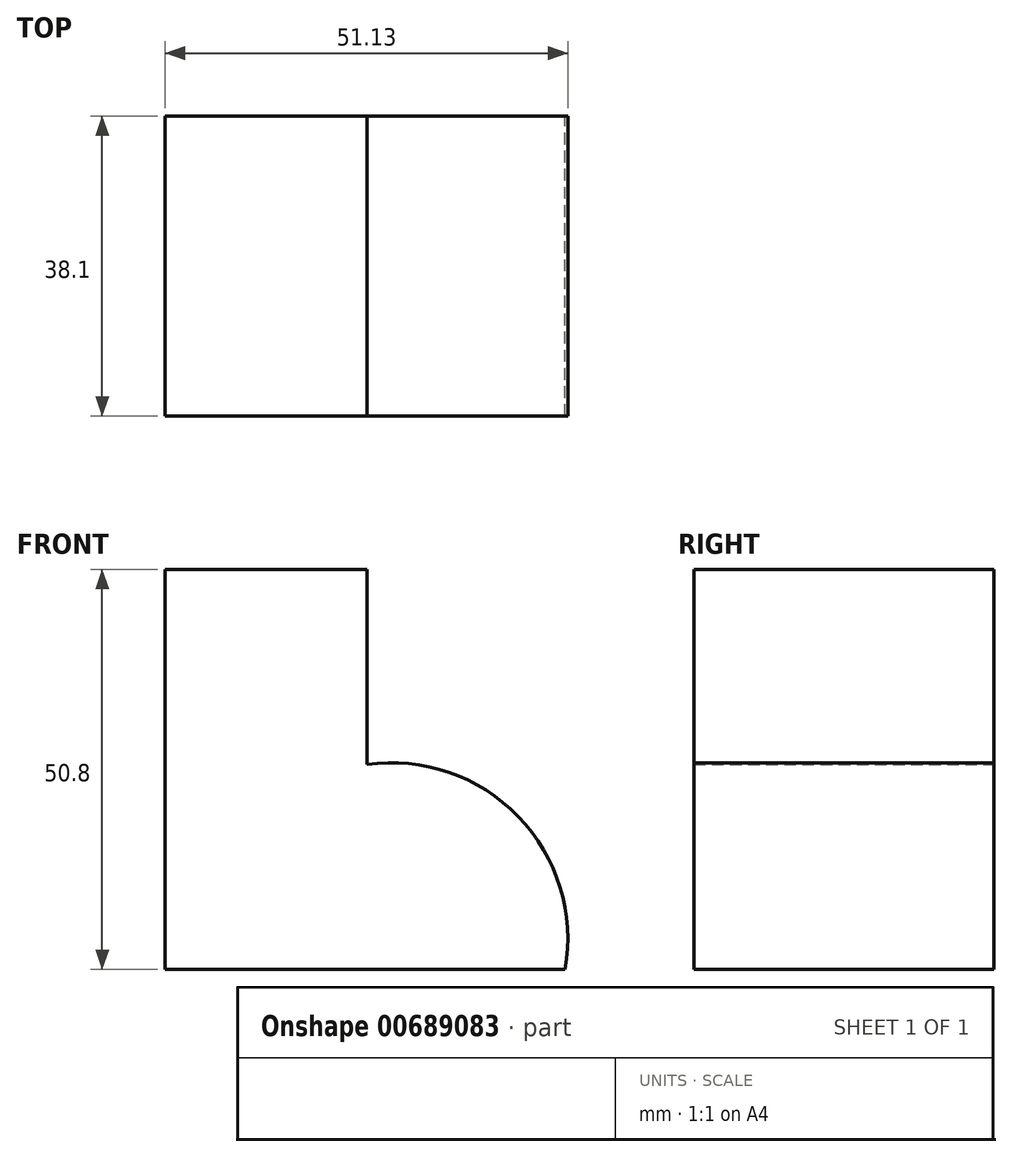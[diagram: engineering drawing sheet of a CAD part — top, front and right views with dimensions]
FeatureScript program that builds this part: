
annotation { "Feature Type Name" : "Feature", "Feature Type Description" : "" }
export const myFeature = defineFeature(function(context is Context, id is Id, definition is map)
    precondition{}
    {
        {
            var Q0;
            Q0=qCreatedBy(makeId("Front.planeOp"),FACE);
            var sketch = newSketch(context, id + "F0", { "sketchPlane" : qUnion([Q0])});
            skLineSegment(sketch, "E0", {"start": v(0, 0) * mm, "end": v(-50.8, 0) * mm});
            skLineSegment(sketch, "E1", {"start": v(-50.8, 0) * mm, "end": v(-50.8, 50.8) * mm});
            skLineSegment(sketch, "E2", {"start": v(-50.8, 50.8) * mm, "end": v(-25.18, 50.8) * mm});
            skLineSegment(sketch, "E3", {"start": v(-25.18, 50.8) * mm, "end": v(-25.18, 26.05) * mm});
            skArc(sketch, "E4", {"start": v(0, 0) * mm, "mid": v(-5.97, 19.43) * mm, "end": v(-25.18, 26.05) * mm});
            skSolve(sketch);
        }
        {
            var Q0;
            Q0=makeQuery(id+"F0.imprint","IMPRINT",FACE,{"disambiguationData":[TD([[makeQuery(id+"F0.imprint","IMPRINT",EDGE,{"derivedFrom":sQuery(id+"F0.wireOp",EDGE,"E0")}),-1.0]])]});
            extrude(context, id + "F1", {"entities" : qUnion([Q0]), "depth" : 38.1 * mm, "offsetDistance" : 25.4 * mm});
        }
    });
